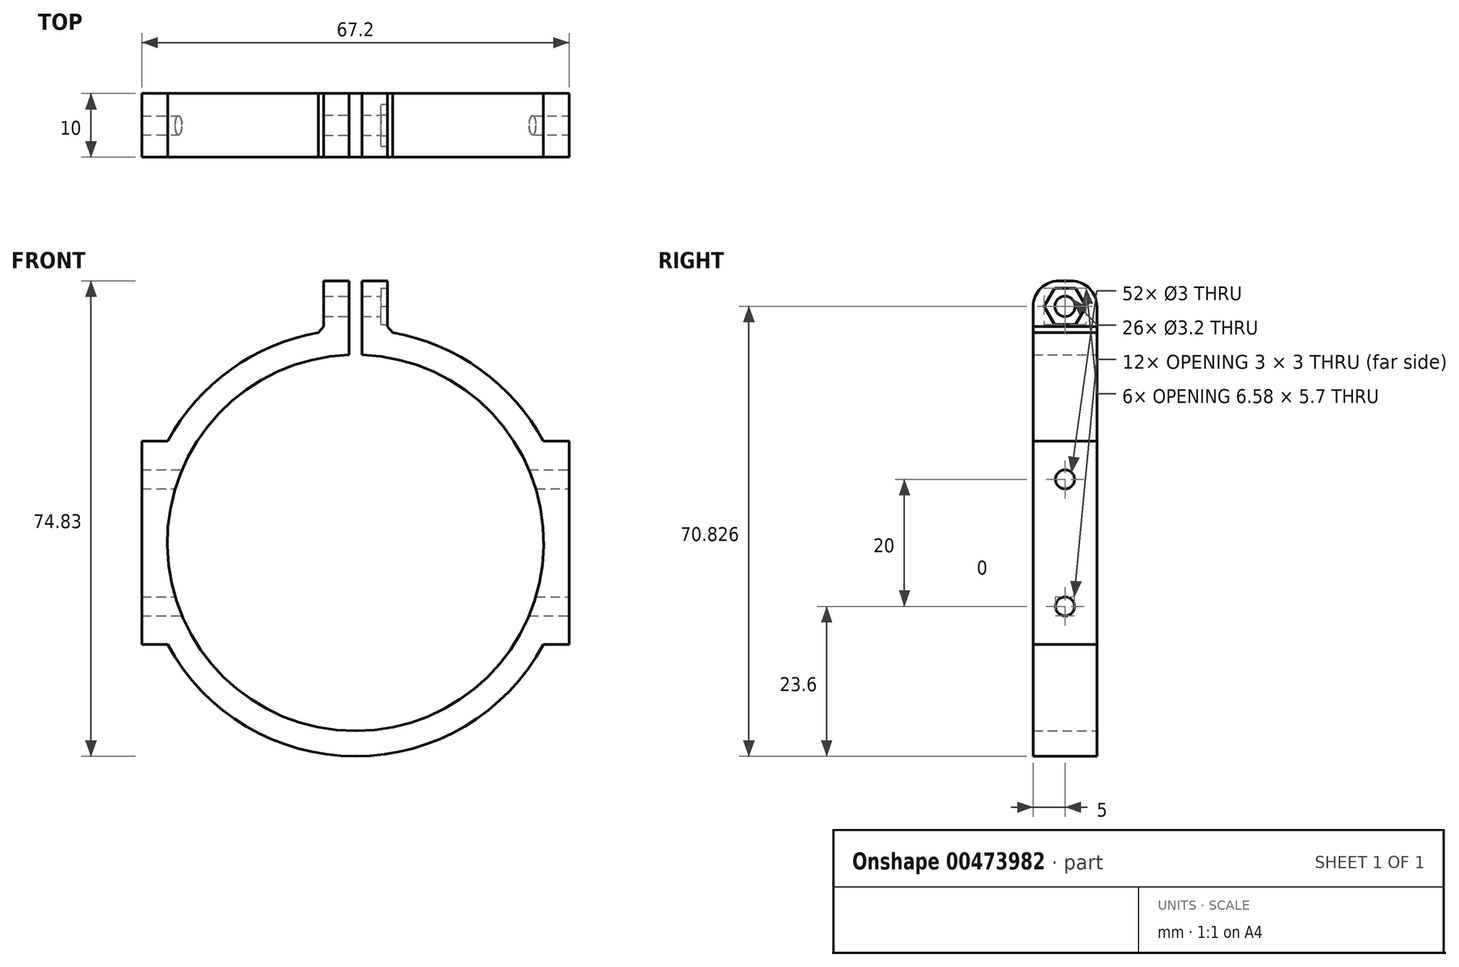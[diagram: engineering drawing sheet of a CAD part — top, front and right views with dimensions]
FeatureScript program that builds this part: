
annotation { "Feature Type Name" : "Feature", "Feature Type Description" : "" }
export const myFeature = defineFeature(function(context is Context, id is Id, definition is map)
    precondition{}
    {
        {
            var Q0;
            Q0=qCreatedBy(makeId("Front.planeOp"),FACE);
            var sketch = newSketch(context, id + "F0", { "sketchPlane" : qUnion([Q0])});
            skArc(sketch, "E0", {"start": v(-1, 29.58) * mm, "mid": v(0, -29.6) * mm, "end": v(1, 29.58) * mm});
            skLineSegment(sketch, "E1.bottom", {"start": v(33.6, -16) * mm, "end": v(29.55, -16) * mm});
            skLineSegment(sketch, "E1.top", {"start": v(33.6, 16) * mm, "end": v(29.55, 16) * mm});
            skLineSegment(sketch, "E1.left", {"start": v(33.6, -16) * mm, "end": v(33.6, 16) * mm});
            skLineSegment(sketch, "E1.right", {"start": v(-33.6, -16) * mm, "end": v(-33.6, 16) * mm});
            skArc(sketch, "E2", {"start": v(-29.55, -16) * mm, "mid": v(0, -33.6) * mm, "end": v(29.55, -16) * mm});
            skLineSegment(sketch, "E3.trimOffspring", {"start": v(-29.55, 16) * mm, "end": v(-33.6, 16) * mm});
            skLineSegment(sketch, "E4.trimOffspring", {"start": v(-29.55, -16) * mm, "end": v(-33.6, -16) * mm});
            skArc(sketch, "E5.trimOffspring", {"start": v(29.55, 16) * mm, "mid": v(19.3, 27.5) * mm, "end": v(5, 33.23) * mm});
            skLineSegment(sketch, "E6.bottom", {"start": v(-5, 41.23) * mm, "end": v(-1, 41.23) * mm});
            skLineSegment(sketch, "E6.left", {"start": v(-5, 41.23) * mm, "end": v(-5, 33.23) * mm});
            skLineSegment(sketch, "E6.right", {"start": v(-1, 41.23) * mm, "end": v(-1, 29.58) * mm});
            skArc(sketch, "E7.trimOffspring", {"start": v(-5, 33.23) * mm, "mid": v(-19.3, 27.5) * mm, "end": v(-29.55, 16) * mm});
            skLineSegment(sketch, "E8.bottom", {"start": v(5, 41.23) * mm, "end": v(1, 41.23) * mm});
            skLineSegment(sketch, "E8.left", {"start": v(5, 41.23) * mm, "end": v(5, 33.23) * mm});
            skLineSegment(sketch, "E8.right", {"start": v(1, 41.23) * mm, "end": v(1, 29.58) * mm});
            skSolve(sketch);
        }
        {
            var Q0;
            Q0 = qSketchRegion(id + "F0", true);
            extrude(context, id + "F1", {"entities" : qUnion([Q0]), "depth" : 10 * mm});
        }
        {
            var Q0;
            Q0=makeQuery(id+"F1.opExtrude","SWEPT_FACE",FACE,{"disambiguationData":[OSD([sQuery(id+"F0.wireOp",EDGE,"E1.left")])]});
            var sketch = newSketch(context, id + "F2", { "sketchPlane" : qUnion([Q0])});
            skCircle(sketch, "E9", {"center": v(-5, 10) * mm, "radius": 1.5 * mm});
            skCircle(sketch, "E10", {"center": v(-5, -10) * mm, "radius": 1.5 * mm});
            skPoint(sketch, "E11", {"position": v(-5, 16) * mm});
            skSolve(sketch);
        }
        {
            var Q0;
            Q0=makeQuery(id+"F2.imprint","IMPRINT",FACE,{"disambiguationData":[TD([[makeQuery(id+"F2.imprint","IMPRINT",EDGE,{"derivedFrom":sQuery(id+"F2.wireOp",EDGE,"E9")}),1.0]])]});
            var Q1;
            Q1=makeQuery(id+"F2.imprint","IMPRINT",FACE,{"disambiguationData":[TD([[makeQuery(id+"F2.imprint","IMPRINT",EDGE,{"derivedFrom":sQuery(id+"F2.wireOp",EDGE,"E10")}),1.0]])]});
            extrude(context, id + "F3", {"entities" : qUnion([Q0, Q1]), "operationType" : NewBodyOperationType.REMOVE, "endBound" : BoundingType.THROUGH_ALL, "oppositeDirection" : true, "depth" : 25 * mm});
        }
        {
            var Q0;
            Q0=makeQuery(id+"F1.opExtrude","SWEPT_FACE",FACE,{"disambiguationData":[OSD([sQuery(id+"F0.wireOp",EDGE,"E8.left")])]});
            var sketch = newSketch(context, id + "F4", { "sketchPlane" : qUnion([Q0])});
            skCircle(sketch, "E12.cCircle", {"center": v(-5, 37.23) * mm, "radius": 2.85 * mm, "construction": true});
            skPoint(sketch, "E12.cCircle.centerSnap0", {"position": v(-10, 37.23) * mm});
            skPoint(sketch, "E12.cCircle.centerSnap1", {"position": v(-5, 41.23) * mm});
            skLineSegment(sketch, "E12.0", {"start": v(-3.35, 40.08) * mm, "end": v(-1.7, 37.23) * mm});
            skLineSegment(sketch, "E12.1", {"start": v(-1.7, 37.23) * mm, "end": v(-3.35, 34.38) * mm});
            skLineSegment(sketch, "E12.2", {"start": v(-3.35, 34.38) * mm, "end": v(-6.65, 34.38) * mm});
            skLineSegment(sketch, "E12.3", {"start": v(-6.65, 34.38) * mm, "end": v(-8.3, 37.23) * mm});
            skLineSegment(sketch, "E12.4", {"start": v(-8.3, 37.23) * mm, "end": v(-6.65, 40.08) * mm});
            skLineSegment(sketch, "E12.5", {"start": v(-6.65, 40.08) * mm, "end": v(-3.35, 40.08) * mm});
            skPoint(sketch, "E12.0.midPoint", {"position": v(-2.53, 38.65) * mm});
            skSolve(sketch);
        }
        {
            var Q0;
            Q0 = qSketchRegion(id + "F4", true);
            extrude(context, id + "F5", {"entities" : qUnion([Q0]), "operationType" : NewBodyOperationType.REMOVE, "oppositeDirection" : true, "depth" : 1 * mm});
        }
        {
            var Q0;
            Q0=sQuery(id+"F4.wireOp",VERTEX,"E12.cCircle.center");
            var Q1;
            Q1=makeQuery(id+"F1.opExtrude","SWEPT_BODY",BODY,{"disambiguationData":[OSD([sQuery(id+"F0.wireOp",EDGE,"E0"),sQuery(id+"F0.wireOp",EDGE,"E1.bottom"),sQuery(id+"F0.wireOp",EDGE,"E1.top"),sQuery(id+"F0.wireOp",EDGE,"E1.left"),sQuery(id+"F0.wireOp",EDGE,"E1.right"),sQuery(id+"F0.wireOp",EDGE,"E2"),sQuery(id+"F0.wireOp",EDGE,"E3.trimOffspring"),sQuery(id+"F0.wireOp",EDGE,"E4.trimOffspring"),sQuery(id+"F0.wireOp",EDGE,"E5.trimOffspring"),sQuery(id+"F0.wireOp",EDGE,"E6.bottom"),sQuery(id+"F0.wireOp",EDGE,"E6.left"),sQuery(id+"F0.wireOp",EDGE,"E6.right"),sQuery(id+"F0.wireOp",EDGE,"E7.trimOffspring"),sQuery(id+"F0.wireOp",EDGE,"E8.bottom"),sQuery(id+"F0.wireOp",EDGE,"E8.left"),sQuery(id+"F0.wireOp",EDGE,"E8.right")])]});
            hole(context, id + "F6", {"style" : HoleStyle.SIMPLE, "endStyle" : HoleEndStyle.THROUGH, "holeDiameter" : 3.2 * mm, "tappedDepth" : 12 * mm, "tapClearance" : 3, "locations" : qUnion([Q0]), "scope" : qUnion([Q1])});
        }
        {
            var Q0;
            Q0=makeQuery(id+"F1.opExtrude","CAP_EDGE",EDGE,{"disambiguationData":[OSD([sQuery(id+"F0.wireOp",EDGE,"E8.bottom")])],"isStart":true});
            var Q1;
            Q1=makeQuery(id+"F1.opExtrude","CAP_EDGE",EDGE,{"disambiguationData":[OSD([sQuery(id+"F0.wireOp",EDGE,"E8.bottom")])],"isStart":false});
            var Q2;
            Q2=makeQuery(id+"F1.opExtrude","CAP_EDGE",EDGE,{"disambiguationData":[OSD([sQuery(id+"F0.wireOp",EDGE,"E6.bottom")])],"isStart":false});
            var Q3;
            Q3=makeQuery(id+"F1.opExtrude","CAP_EDGE",EDGE,{"disambiguationData":[OSD([sQuery(id+"F0.wireOp",EDGE,"E6.bottom")])],"isStart":true});
            fillet(context, id + "F7", {"entities" : qUnion([Q0, Q1, Q2, Q3]), "radius" : 4 * mm, "tangentPropagation" : true, "allowEdgeOverflow" : false});
        }
        {
            var Q0;
            Q0=makeQuery(id+"F1.opExtrude","SWEPT_EDGE",EDGE,{"disambiguationData":[OSD([sQuery(id+"F0.wireOp",EDGE,"E5.trimOffspring"),sQuery(id+"F0.wireOp",EDGE,"E8.left")])]});
            var Q1;
            Q1=makeQuery(id+"F1.opExtrude","SWEPT_EDGE",EDGE,{"disambiguationData":[OSD([sQuery(id+"F0.wireOp",EDGE,"E6.left"),sQuery(id+"F0.wireOp",EDGE,"E7.trimOffspring")])]});
            chamfer(context, id + "F8", {"entities" : qUnion([Q0, Q1]), "width" : 1 * mm, "tangentPropagation" : true});
        }
    });
